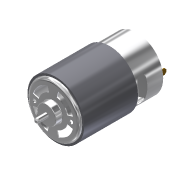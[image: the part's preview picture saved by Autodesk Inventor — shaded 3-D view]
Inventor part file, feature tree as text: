
AUTODESK INVENTOR PART (.ipt)
format: ipt  version: 2011 (Build 150239000, 239)  size: 328,192 bytes
history: native  units: mm (DEFAULTED — no unit token found)
features: sketch x15, extrude x13, fillet x3, plane x3, hole x2, mirror x2, pattern_circular x2, shell x1, chamfer x1
ambient origin geometry x8: Origin, YZ Plane, XZ Plane, XY Plane, X Axis, Y Axis, Z Axis, Center Point
bodies: Solid1 (feature_tree)
feature tree (42):
  extrude  "Extrusion1"  Depth=57.0mm TaperAngle=0.0deg
  fillet  "Fillet1"  Radius=2.0mm
  shell  "Shell1"  Thickness=0.62mm
  extrude  "Extrusion2"  Depth=4.5mm TaperAngle=0.0deg
  fillet  "Fillet2"  Radius=0.5mm
  extrude  "Extrusion3"  Depth=7.6mm TaperAngle=0.0deg
  fillet  "Fillet3"  Radius=1.6mm
  hole  "Hole1"  [1 undecoded]
  mirror  "Mirror1"
  extrude  "Extrusion4"  Depth=14.0mm
  pattern_circular  "Circular Pattern1"  Count=4 Angle=360.0deg
  plane  "Work Plane1"
  extrude  "Extrusion5"  Depth=0.62mm TaperAngle=0.0deg
  extrude  "Extrusion6"  Depth=0.62mm TaperAngle=0.0deg
  extrude  "Extrusion7"  Depth=3.0mm TaperAngle=0.0deg
  extrude  "Extrusion8"  Depth=0.8mm TaperAngle=0.0deg
  extrude  "Extrusion9"  Depth=1.0mm TaperAngle=0.0deg
  extrude  "Extrusion10"  Depth=3.15mm
  pattern_circular  "Circular Pattern2"  [2 undecoded]
  extrude  "Extrusion11"  Depth=1.0mm TaperAngle=0.0deg
  chamfer  "Chamfer1"  Distance=40.0mm Angle=360.0deg
  hole  "Hole2"  [1 undecoded]
  mirror  "Mirror2"
  plane  "Work Plane2"
  extrude  "Extrusion12"  Depth=3.8mm
  plane  "Work Plane3"
  extrude  "Flux Ring"  Depth=14.0mm
  sketch  "Sketch1"  dims[d0=35.8mm d1=57.0mm d2=0.0mm d3=2.0mm d4=0.62mm]
  sketch  "Sketch2"  dims[d5=13.0mm d6=4.5mm d7=0.0mm d8=0.5mm]
  sketch  "Sketch3"  dims[d9=3.2mm d10=7.6mm d11=0.0mm d12=1.6mm]
  sketch  "Sketch4"  dims[d13=12.5mm]
  sketch  "Sketch5"  dims[d14=2.5mm d15=6.0mm d16=4.0mm d17=2.0mm d18=14.3117mm d19=8.0mm d20=20.594885mm d21=15.0deg]
  sketch  "Sketch6"  dims[d22=15.0deg d23=14.0mm]
  sketch  "Sketch7"  dims[d24=10.0mm]
  sketch  "Sketch8"  dims[d25=10.0mm d26=0.0mm d27=40.0mm d29=360.0deg]
  sketch  "Sketch9"  dims[d30=-1.75mm d31=0.62mm d32=0.0mm]
  sketch  "Sketch10"  dims[d33=24.0mm d34=0.62mm d35=0.0mm]
  sketch  "Sketch11"  dims[d36=10.75mm d37=3.0mm d38=0.0mm]
  sketch  "Sketch12"  dims[d39=6.9mm d40=0.8mm d41=0.0mm]
  sketch  "Sketch13"  dims[d42=3.2mm d43=1.0mm d44=0.0mm]
  sketch  "Sketch14"  dims[d45=3.15mm d46=3.15mm]
  sketch  "Sketch15"  dims[d47=9.875mm d48=6.5mm d49=1.0mm d50=0.0mm d51=40.0mm d53=360.0deg d54=0.5mm d55=3.8mm d56=14.0mm d57=7.2mm d58=0.0mm d59=1.0mm d60=2.0mm d61=3.0mm d62=2.0mm d63=6.0mm d64=4.0mm d65=2.0mm d66=14.3117mm d67=1.0mm d68=20.594885mm d69=18.0mm d70=10.75mm d71=5.9mm d72=12.0mm d73=7.2mm d74=0.0mm d75=45.0deg d76=1.35mm d77=36.5mm d78=0.0mm]
note: 4 required parameter values undecoded (feature->parameter linkage not recoverable at this tier; creation-order binding heuristic only, values carry confidence <= 0.55)
